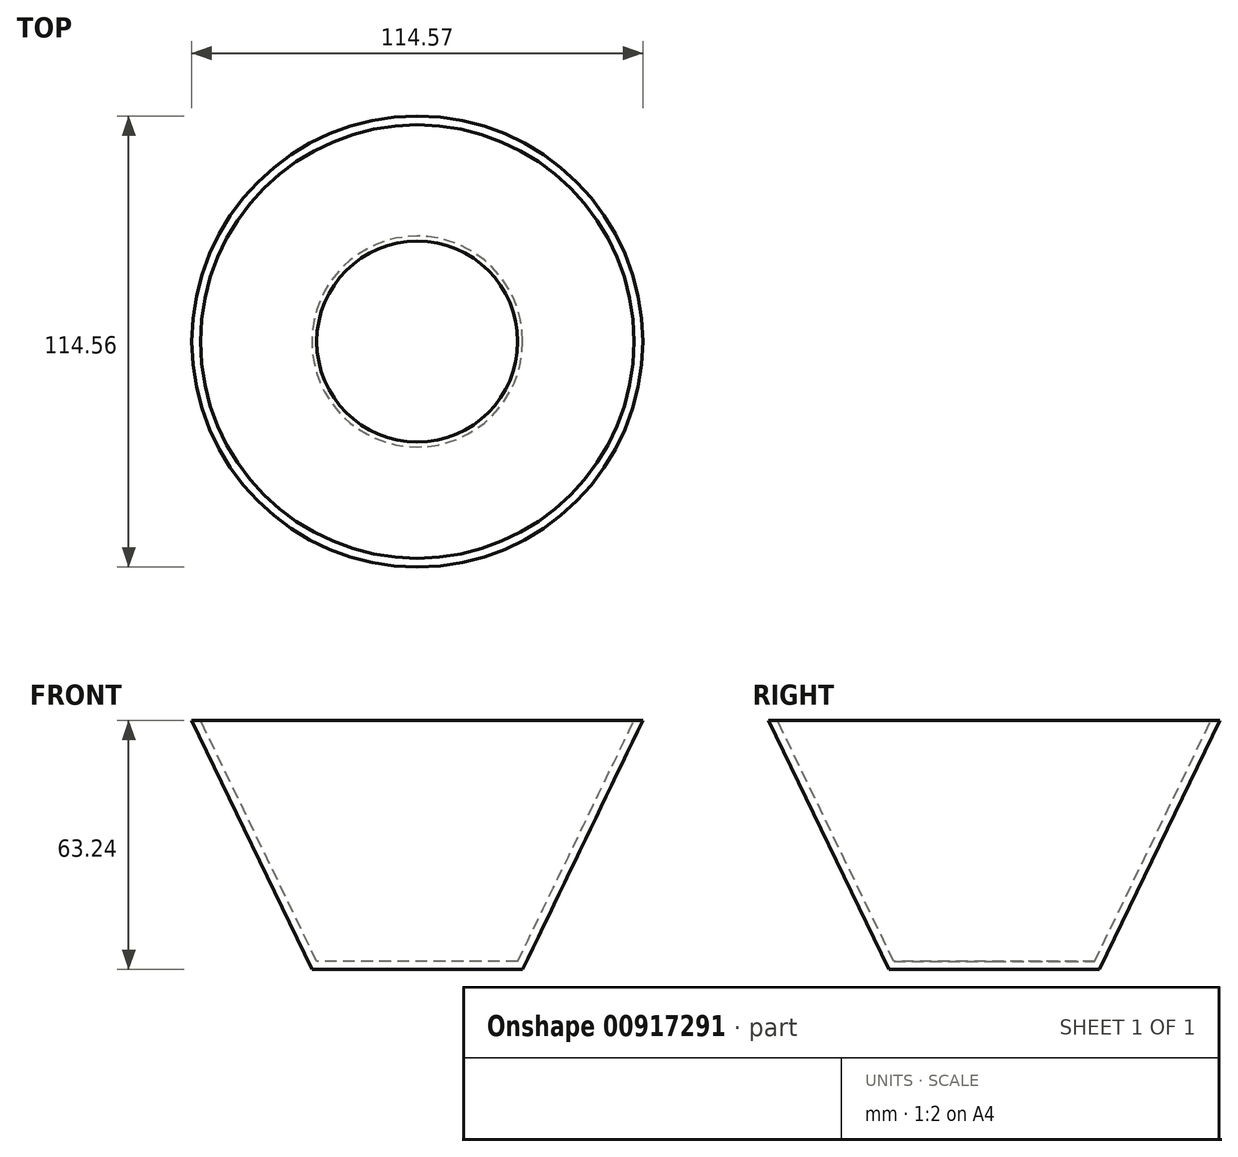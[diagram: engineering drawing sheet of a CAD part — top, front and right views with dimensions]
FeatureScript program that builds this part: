
annotation { "Feature Type Name" : "Feature", "Feature Type Description" : "" }
export const myFeature = defineFeature(function(context is Context, id is Id, definition is map)
    precondition{}
    {
        {
            var Q0;
            Q0=qCreatedBy(makeId("Front.planeOp"),FACE);
            var sketch = newSketch(context, id + "F0", { "sketchPlane" : qUnion([Q0])});
            skLineSegment(sketch, "E0", {"start": v(87.38, 75.12) * mm, "end": v(87.38, 11.88) * mm});
            skLineSegment(sketch, "E1", {"start": v(87.38, 11.88) * mm, "end": v(114.17, 11.88) * mm});
            skLineSegment(sketch, "E2", {"start": v(114.17, 11.88) * mm, "end": v(144.67, 75.12) * mm});
            skLineSegment(sketch, "E3", {"start": v(144.67, 75.12) * mm, "end": v(87.38, 75.12) * mm});
            skSolve(sketch);
        }
        {
            var Q0;
            Q0 = qSketchRegion(id + "F0", true);
            var Q1;
            Q1=sQuery(id+"F0.wireOp",EDGE,"E0");
            revolve(context, id + "F1", {"surfaceOperationType" : NewSurfaceOperationType.NEW, "entities" : qUnion([Q0]), "axis" : qUnion([Q1]), "revolveType" : RevolveType.FULL});
        }
        {
            var Q0;
            Q0=makeQuery(id+"F1.opRevolve","SWEPT_FACE",FACE,{"disambiguationData":[OSD([sQuery(id+"F0.wireOp",EDGE,"E3")])]});
            shell(context, id + "F2", {"entities" : qUnion([Q0]), "thickness" : 2 * mm});
        }
    });
